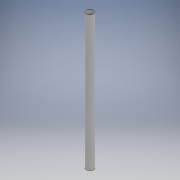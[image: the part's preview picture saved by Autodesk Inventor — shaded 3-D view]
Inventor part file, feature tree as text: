
AUTODESK INVENTOR PART (.ipt)
format: ipt  version: 2018.3 (Build 223284000, 284)  size: 92,160 bytes
history: native  units: mm
features: extrude x1, sketch x1
ambient origin geometry x8: Origin, YZ Plane, XZ Plane, XY Plane, X Axis, Y Axis, Z Axis, Center Point
bodies: Solid1 (feature_tree)
feature tree (2):
  extrude  "Extrusion1"  Depth=150.0mm
  sketch  "Sketch1"  dims[d0=8.0mm d1=7.0mm d2=150.0mm d3=0.0mm]
